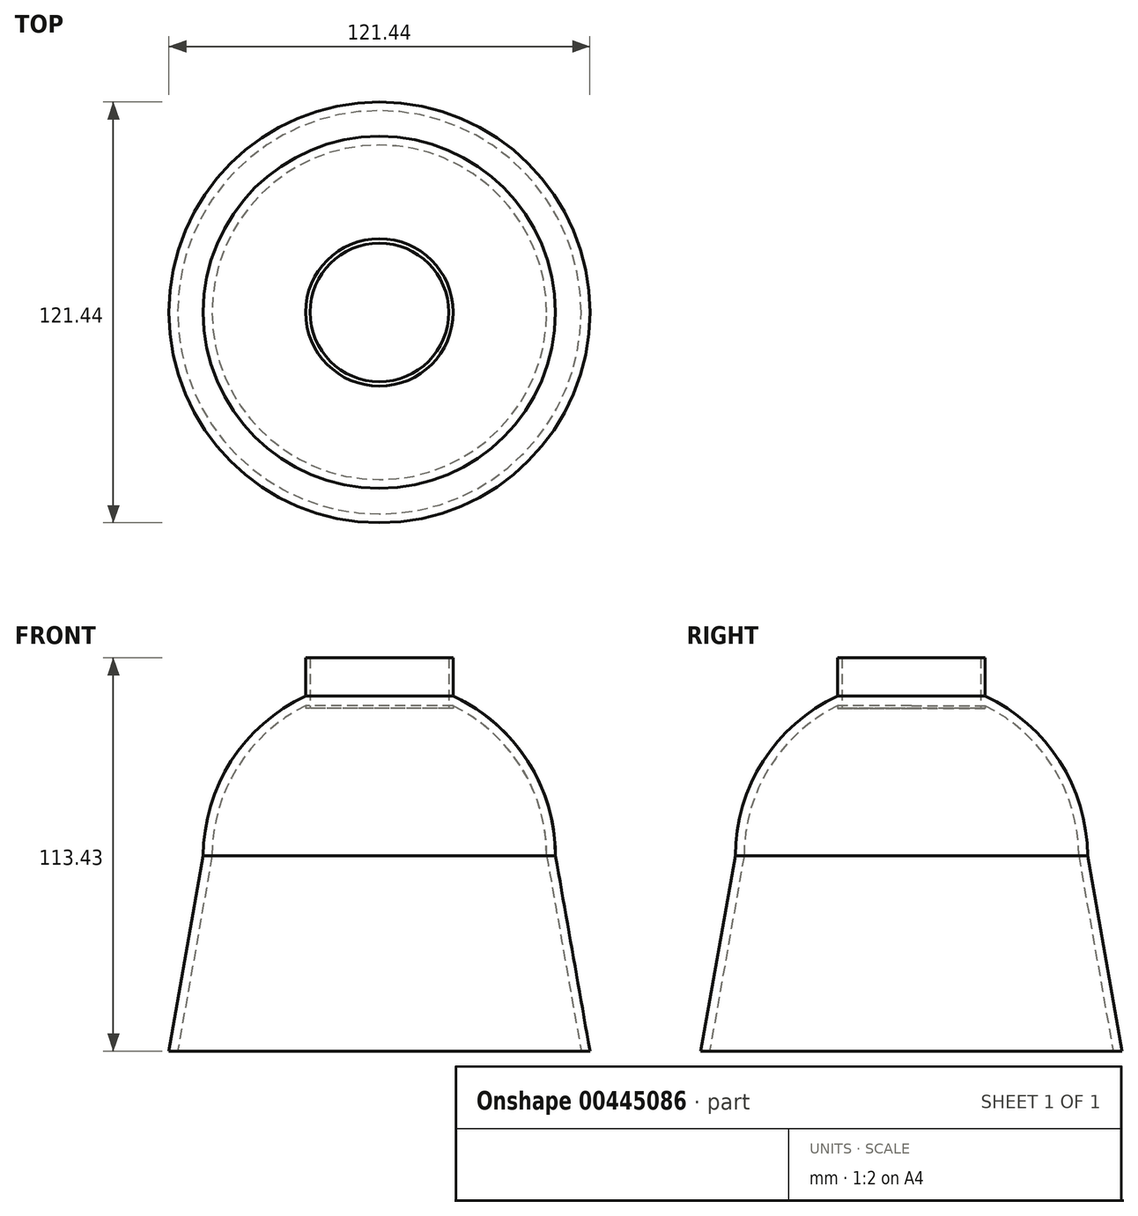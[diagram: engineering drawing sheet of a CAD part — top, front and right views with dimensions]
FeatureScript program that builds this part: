
annotation { "Feature Type Name" : "Feature", "Feature Type Description" : "" }
export const myFeature = defineFeature(function(context is Context, id is Id, definition is map)
    precondition{}
    {
        {
            var Q0;
            Q0=qCreatedBy(makeId("Front.planeOp"),FACE);
            var sketch = newSketch(context, id + "F0", { "sketchPlane" : qUnion([Q0])});
            skArc(sketch, "E0", {"start": v(0, 50.8) * mm, "mid": v(-35.92, 35.92) * mm, "end": v(-50.8, 0) * mm});
            skArc(sketch, "E1", {"start": v(0, 48.26) * mm, "mid": v(-34.12, 34.12) * mm, "end": v(-48.26, 0) * mm});
            skLineSegment(sketch, "E2.bottom", {"start": v(-48.26, 0) * mm, "end": v(-50.8, 0) * mm});
            skPoint(sketch, "E3.bottom.start.orphan", {"position": v(48.26, 0) * mm});
            skLineSegment(sketch, "E4", {"start": v(0, 50.8) * mm, "end": v(0, 48.26) * mm});
            skLineSegment(sketch, "E5", {"start": v(-48.26, 0) * mm, "end": v(-58.18, -56.28) * mm});
            skLineSegment(sketch, "E6", {"start": v(-50.8, 0) * mm, "end": v(-60.72, -56.28) * mm});
            skLineSegment(sketch, "E7", {"start": v(-58.18, -56.28) * mm, "end": v(-60.72, -56.28) * mm});
            skLineSegment(sketch, "E8", {"start": v(0, 50.8) * mm, "end": v(0, -56.28) * mm, "construction": true});
            skPoint(sketch, "E8.endSnap0", {"position": v(0, 49.53) * mm});
            skLineSegment(sketch, "E9", {"start": v(-60.72, -56.28) * mm, "end": v(0, -56.28) * mm, "construction": true});
            skLineSegment(sketch, "E10", {"start": v(-48.26, 0) * mm, "end": v(-48.26, -56.28) * mm, "construction": true});
            skSolve(sketch);
        }
        {
            var Q0;
            Q0=makeQuery(id+"F0.imprint","IMPRINT",FACE,{"disambiguationData":[TD([[makeQuery(id+"F0.imprint","IMPRINT",EDGE,{"derivedFrom":sQuery(id+"F0.wireOp",EDGE,"E0")}),1.0]])]});
            var Q1;
            Q1=makeQuery(id+"F0.imprint","IMPRINT",FACE,{"disambiguationData":[TD([[makeQuery(id+"F0.imprint","IMPRINT",EDGE,{"derivedFrom":sQuery(id+"F0.wireOp",EDGE,"E2.bottom")}),1.0]])]});
            var Q2;
            Q2=sQuery(id+"F0.wireOp",EDGE,"E8");
            revolve(context, id + "F1", {"entities" : qUnion([Q0, Q1]), "axis" : qUnion([Q2]), "revolveType" : RevolveType.FULL});
        }
        {
            var Q0;
            Q0=qCreatedBy(makeId("Top.planeOp"),FACE);
            var sketch = newSketch(context, id + "F2", { "sketchPlane" : qUnion([Q0])});
            skCircle(sketch, "E11", {"center": v(0, 0) * mm, "radius": 20 * mm});
            skCircle(sketch, "E12", {"center": v(0, 0) * mm, "radius": 21.27 * mm});
            skSolve(sketch);
        }
        {
            var Q0;
            Q0 = qSketchRegion(id + "F2", true);
            extrude(context, id + "F3", {"entities" : qUnion([Q0]), "operationType" : NewBodyOperationType.ADD, "depth" : 57.15 * mm});
        }
        {
            var Q0;
            Q0=makeQuery(id+"F2.imprint","IMPRINT",FACE,{"disambiguationData":[TD([[makeQuery(id+"F2.imprint","IMPRINT",EDGE,{"derivedFrom":sQuery(id+"F2.wireOp",EDGE,"E11")}),1.0]])]});
            extrude(context, id + "F4", {"entities" : qUnion([Q0]), "operationType" : NewBodyOperationType.REMOVE, "endBound" : BoundingType.THROUGH_ALL, "depth" : 82.55 * mm});
        }
        {
            var Q0;
            Q0=makeQuery(id+"F2.imprint","IMPRINT",FACE,{"disambiguationData":[TD([[makeQuery(id+"F2.imprint","IMPRINT",EDGE,{"derivedFrom":sQuery(id+"F2.wireOp",EDGE,"E11")}),1.0]])]});
            var Q1;
            Q1=makeQuery(id+"F2.imprint","IMPRINT",FACE,{"disambiguationData":[TD([[makeQuery(id+"F2.imprint","IMPRINT",EDGE,{"derivedFrom":sQuery(id+"F2.wireOp",EDGE,"E11")}),-1.0]])]});
            extrude(context, id + "F5", {"entities" : qUnion([Q0, Q1]), "operationType" : NewBodyOperationType.REMOVE, "depth" : 42.55 * mm});
        }
    });
